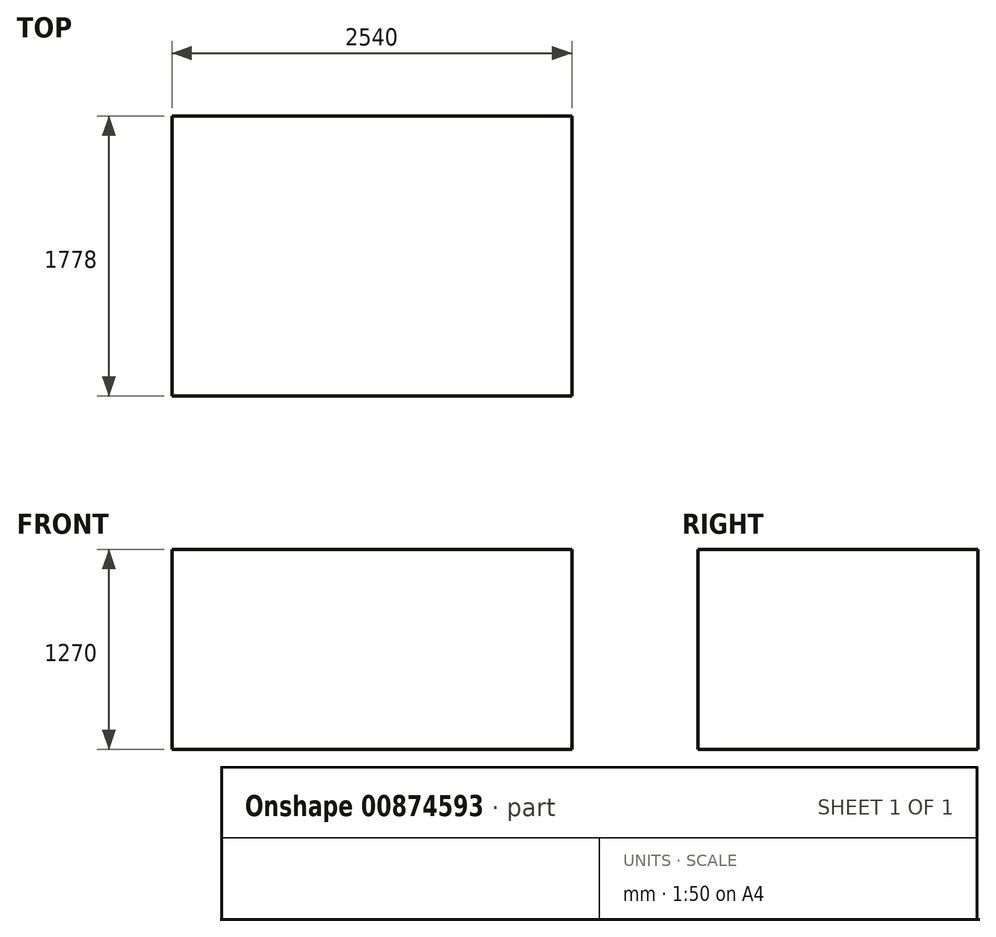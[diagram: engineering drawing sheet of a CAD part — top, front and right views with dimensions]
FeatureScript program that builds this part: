
annotation { "Feature Type Name" : "Feature", "Feature Type Description" : "" }
export const myFeature = defineFeature(function(context is Context, id is Id, definition is map)
    precondition{}
    {
        {
            var Q0;
            Q0=qCreatedBy(makeId("Top.planeOp"),FACE);
            var sketch = newSketch(context, id + "F0", { "sketchPlane" : qUnion([Q0])});
            skLineSegment(sketch, "E0.bottom", {"start": v(-57.77, -52.15) * mm, "end": v(2482.23, -52.15) * mm});
            skLineSegment(sketch, "E0.top", {"start": v(-57.77, 1725.85) * mm, "end": v(2482.23, 1725.85) * mm});
            skLineSegment(sketch, "E0.left", {"start": v(-57.77, -52.15) * mm, "end": v(-57.77, 1725.85) * mm});
            skLineSegment(sketch, "E0.right", {"start": v(2482.23, -52.15) * mm, "end": v(2482.23, 1725.85) * mm});
            skSolve(sketch);
        }
        {
            var Q0;
            Q0=makeQuery(id+"F0.imprint","IMPRINT",FACE,{"disambiguationData":[TD([[makeQuery(id+"F0.imprint","IMPRINT",EDGE,{"derivedFrom":sQuery(id+"F0.wireOp",EDGE,"E0.bottom")}),1.0]])]});
            extrude(context, id + "F1", {"entities" : qUnion([Q0]), "depth" : 1270 * mm, "offsetDistance" : 25.4 * mm});
        }
    });
